# Revit family: 28_CC_MOD_balk_UNP180
name_source: partatom
category: Structural Framing
revit_build: Autodesk Revit 2017 (Build: 20181011_1645(x64)
units: mm (PartAtom-declared; Revit-internal decimal feet)

## family parameters
Always export as geometry = No
Always vertical = No
Cut with Voids When Loaded = No
Material for Model Behavior = Steel
Section Shape = Not Defined
Shared = No
Show family pre-cut in plan views = Yes

## types (1)
- H
    A = 0.01 m²
    NL_28_hulp_maat = 115 mm
    NL_28_max_extensie = 1000 mm  [stored 3.28084 ft]
    Structural Material = Metal - Steel - 345 MPa
    W = 0.35402
    bf = 240 mm  [stored 0.787402 ft]
    d = 240 mm  [stored 0.787402 ft]
    k = 25 mm  [stored 0.082021 ft]
    tf = 10 mm  [stored 0.0328084 ft]
    tr = 15 mm  [stored 0.0492126 ft]
    tw = 7 mm  [stored 0.0229659 ft]

note: [stored X ft] marks values corroborated as IEEE doubles in the binary element streams (Revit-internal decimal feet)

## geometry (parser evidence)
native form markers: Sweep x2
no freeform markers — native parametric forms only
